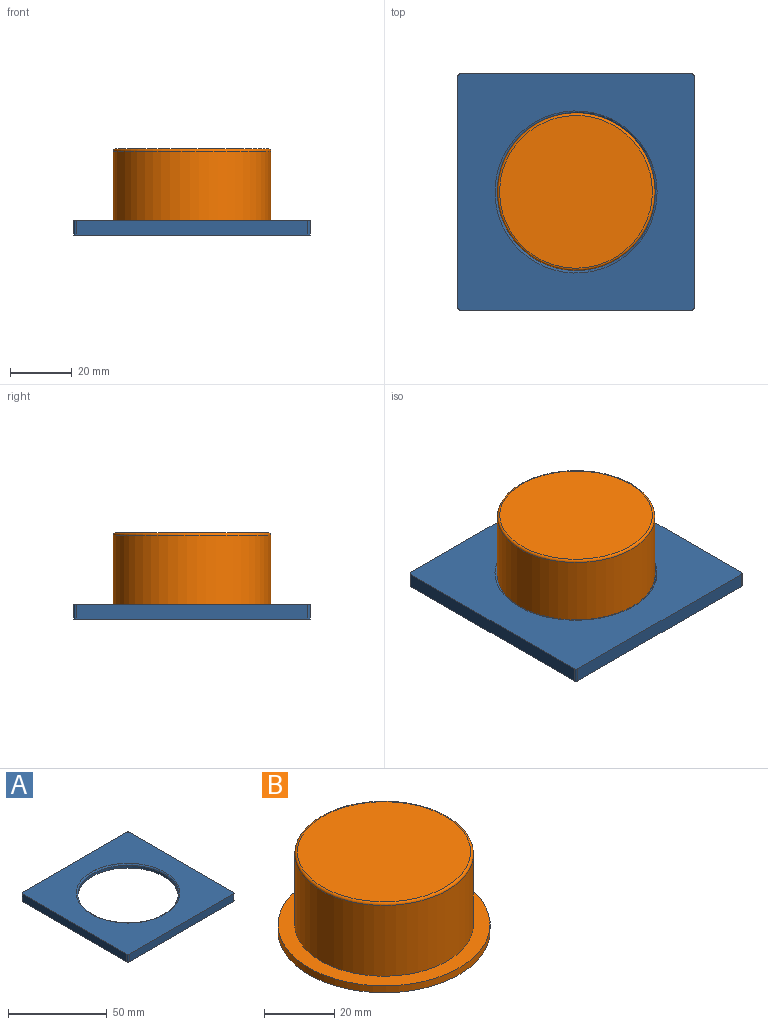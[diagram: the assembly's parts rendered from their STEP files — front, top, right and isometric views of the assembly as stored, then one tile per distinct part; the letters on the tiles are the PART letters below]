
ASSEMBLY  parts=2 mates=1
PART A: 14 faces, bbox 76.2x76.2x4.8 mm
  f0: cylinder r=25.4mm len=50.8mm, axis (0,0,-1), area 258.4mm2, adj f8,f13
  f1: plane 74.68x4.76mm, normal (0,1,0), area 355.6mm2, adj f5,f6,f9,f12
  f2: plane 74.68x4.76mm, normal (-1,0,0), area 355.6mm2, adj f5,f6,f9,f10
  f3: plane 74.68x4.76mm, normal (0,-1,0), area 355.6mm2, adj f5,f6,f10,f11
  f4: plane 74.68x4.76mm, normal (1,0,0), area 355.6mm2, adj f5,f6,f11,f12
  f5: plane 76.2x76.2mm, normal (0,0,1), area 3655.7mm2, adj f1,f2,f3,f4,f9,f10,f11,f12
  f6: plane 76.2x76.2mm, normal (0,0,-1), area 2947.8mm2, adj f1,f2,f3,f4,f7,f9,f10,f11
  f7: cylinder r=30.16mm len=60.33mm, axis (0,0,-1), area 451.3mm2, adj f6,f8
  f8: plane 60.33x60.33mm, normal (0,0,-1), area 831.3mm2, adj f0,f7
  f9: cylinder r=0.76mm len=4.76mm, axis (0,0,1), area 5.7mm2, adj f1,f2,f5,f6
  f10: cylinder r=0.76mm len=4.76mm, axis (0,0,-1), area 5.7mm2, adj f2,f3,f5,f6
  f11: cylinder r=0.76mm len=4.76mm, axis (0,0,1), area 5.7mm2, adj f3,f4,f5,f6
  f12: cylinder r=0.76mm len=4.76mm, axis (0,0,-1), area 5.7mm2, adj f1,f4,f5,f6
  f13: torus R=26.16mm, axis (0,0,1), area 193.1mm2, adj f0,f5
PART B: 6 faces, bbox 60.3x60.3x27.8 mm
  f0: cylinder r=30.16mm len=60.33mm, axis (0,0,-1), area 451.3mm2, adj f1,f2
  f1: plane 60.33x60.33mm, normal (0,0,1), area 831.3mm2, adj f0,f3
  f2: plane 60.33x60.33mm, normal (0,0,-1), area 2858.1mm2, adj f0
  f3: cylinder r=25.4mm len=50.8mm, axis (0,0,-1), area 3932.1mm2, adj f1,f5
  f4: plane 49.28x49.28mm, normal (0,0,1), area 1907mm2, adj f5
  f5: torus R=24.64mm, axis (0,0,1), area 188.9mm2, adj f3,f4
PLACE A t=(-42.21,6.24,6.18)mm
PLACE B t=(-10.56,-11.95,6.18)mm
MATE fastened A.f0 <-> B.f0  axis (0,0,-1) through (-26.36,-1.84,8.56)mm
